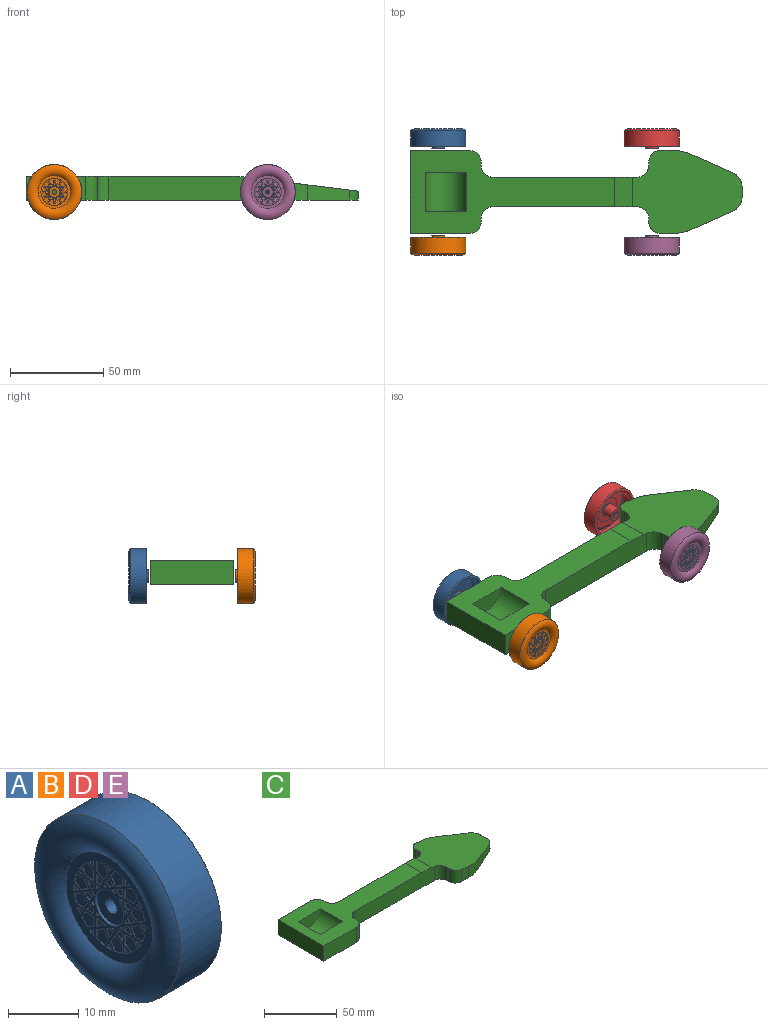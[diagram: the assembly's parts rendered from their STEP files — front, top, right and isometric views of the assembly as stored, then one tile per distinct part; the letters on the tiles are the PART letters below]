
ASSEMBLY  parts=5 mates=3
PART A: 271 faces, bbox 10.7x34x34 mm
  f0: torus R=13.96mm, axis (1,0,0), area 222.7mm2, adj f99,f270
  f1: plane 29.46x29.46mm, normal (-1,0,0), area 2.9mm2, adj f100,f270
  f2: cylinder r=7.18mm len=1.54mm, axis (-1,0,0), area 0.2mm2, adj f27,f86,f101,f256
  f3: cylinder r=7.18mm len=1.05mm, axis (-1,0,0), area 0.1mm2, adj f28,f101,f254,f255
  f4: cylinder r=7.18mm len=1.54mm, axis (-1,0,0), area 0.2mm2, adj f29,f101,f250,f253
  f5: cylinder r=7.18mm len=0.91mm, axis (-1,0,0), area 0.1mm2, adj f30,f101,f248,f249
  f6: cylinder r=7.18mm len=1.13mm, axis (-1,0,0), area 0.2mm2, adj f31,f101,f244,f247
  f7: cylinder r=7.18mm len=0.91mm, axis (-1,0,0), area 0.1mm2, adj f32,f101,f242,f243
  f8: cylinder r=7.18mm len=1.54mm, axis (-1,0,0), area 0.2mm2, adj f33,f101,f238,f241
  f9: cylinder r=7.18mm len=1.05mm, axis (-1,0,0), area 0.1mm2, adj f34,f101,f236,f237
  f10: cylinder r=7.18mm len=1.54mm, axis (-1,0,0), area 0.2mm2, adj f35,f101,f232,f235
  f11: cylinder r=7.18mm len=0.91mm, axis (-1,0,0), area 0.1mm2, adj f36,f101,f230,f231
  f12: cylinder r=7.18mm len=1.13mm, axis (-1,0,0), area 0.2mm2, adj f37,f101,f226,f229
  f13: cylinder r=7.18mm len=0.91mm, axis (-1,0,0), area 0.1mm2, adj f38,f101,f224,f225
  f14: cylinder r=7.18mm len=1.54mm, axis (-1,0,0), area 0.2mm2, adj f39,f101,f220,f223
  f15: cylinder r=7.18mm len=1.05mm, axis (-1,0,0), area 0.1mm2, adj f40,f101,f218,f219
  f16: cylinder r=7.18mm len=1.54mm, axis (-1,0,0), area 0.2mm2, adj f41,f82,f101,f217
  f17: cylinder r=7.18mm len=0.91mm, axis (-1,0,0), area 0.1mm2, adj f65,f101,f118,f139
  f18: cylinder r=7.18mm len=1.13mm, axis (-1,0,0), area 0.2mm2, adj f59,f101,f136,f261
  f19: cylinder r=7.18mm len=1.54mm, axis (-1,0,0), area 0.2mm2, adj f64,f101,f119,f134
  f20: cylinder r=7.18mm len=1.05mm, axis (-1,0,0), area 0.1mm2, adj f53,f101,f132,f133
  f21: cylinder r=7.18mm len=1.54mm, axis (-1,0,0), area 0.2mm2, adj f54,f101,f128,f131
  f22: cylinder r=7.18mm len=0.91mm, axis (-1,0,0), area 0.1mm2, adj f55,f101,f126,f127
  f23: cylinder r=7.18mm len=1.13mm, axis (-1,0,0), area 0.2mm2, adj f56,f101,f125,f142
  f24: cylinder r=7.18mm len=0.91mm, axis (-1,0,0), area 0.1mm2, adj f57,f89,f101,f143
  f25: cylinder r=7.18mm len=0.91mm, axis (-1,0,0), area 0.1mm2, adj f58,f78,f101,f260
  f26: plane 1.41x1.22mm, normal (-1,0,0), area 1.1mm2, adj f85,f146,f147,f258
  f27: plane 2.83x2.32mm, normal (-1,0,0), area 4.5mm2, adj f2,f86,f148,f256,f257
  f28: plane 1.05x0.93mm, normal (-1,0,0), area 0.5mm2, adj f3,f254,f255
  f29: plane 2.83x2.32mm, normal (-1,0,0), area 4.5mm2, adj f4,f250,f251,f252,f253
  f30: plane 1.05x0.91mm, normal (-1,0,0), area 0.5mm2, adj f5,f248,f249
  f31: plane 2.48x2.48mm, normal (-1,0,0), area 4.5mm2, adj f6,f244,f245,f246,f247
  f32: plane 1.05x0.91mm, normal (-1,0,0), area 0.5mm2, adj f7,f242,f243
  f33: plane 2.83x2.32mm, normal (-1,0,0), area 4.5mm2, adj f8,f238,f239,f240,f241
  f34: plane 1.05x0.93mm, normal (-1,0,0), area 0.5mm2, adj f9,f236,f237
  f35: plane 2.83x2.32mm, normal (-1,0,0), area 4.5mm2, adj f10,f232,f233,f234,f235
  f36: plane 1.05x0.91mm, normal (-1,0,0), area 0.5mm2, adj f11,f230,f231
  f37: plane 2.48x2.48mm, normal (-1,0,0), area 4.5mm2, adj f12,f226,f227,f228,f229
  f38: plane 1.05x0.91mm, normal (-1,0,0), area 0.5mm2, adj f13,f224,f225
  f39: plane 2.83x2.32mm, normal (-1,0,0), area 4.5mm2, adj f14,f220,f221,f222,f223
  f40: plane 1.05x0.93mm, normal (-1,0,0), area 0.5mm2, adj f15,f218,f219
  f41: plane 2.83x2.32mm, normal (-1,0,0), area 4.5mm2, adj f16,f82,f152,f216,f217
  f42: plane 0.71x0.45mm, normal (-1,0,0), area 0.2mm2, adj f66,f169,f170,f214,f215
  f43: plane 0.71x0.45mm, normal (-1,0,0), area 0.2mm2, adj f67,f167,f168,f212,f213
  f44: plane 0.52x0.52mm, normal (-1,0,0), area 0.2mm2, adj f68,f165,f166,f210,f211
  f45: plane 0.71x0.45mm, normal (-1,0,0), area 0.2mm2, adj f69,f163,f164,f208,f209
  f46: plane 0.71x0.45mm, normal (-1,0,0), area 0.2mm2, adj f70,f161,f162,f206,f207
  f47: plane 0.52x0.52mm, normal (-1,0,0), area 0.2mm2, adj f71,f159,f160,f204,f205
  f48: plane 0.71x0.45mm, normal (-1,0,0), area 0.2mm2, adj f72,f157,f158,f202,f203
  f49: plane 0.71x0.45mm, normal (-1,0,0), area 0.2mm2, adj f73,f155,f156,f200,f201
  f50: plane 0.52x0.52mm, normal (-1,0,0), area 0.2mm2, adj f74,f87,f144,f145,f154
  f51: plane 1.41x1.22mm, normal (-1,0,0), area 1.1mm2, adj f83,f150,f151,f171
  f52: plane 0.52x0.52mm, normal (-1,0,0), area 0.2mm2, adj f75,f84,f149,f153,f259
  f53: plane 1.05x0.93mm, normal (-1,0,0), area 0.5mm2, adj f20,f132,f133
  f54: plane 2.83x2.32mm, normal (-1,0,0), area 4.5mm2, adj f21,f128,f129,f130,f131
  f55: plane 1.05x0.91mm, normal (-1,0,0), area 0.5mm2, adj f22,f126,f127
  f56: plane 2.48x2.48mm, normal (-1,0,0), area 4.5mm2, adj f23,f88,f108,f125,f142
  f57: plane 1.05x0.91mm, normal (-1,0,0), area 0.5mm2, adj f24,f89,f143
  f58: plane 1.05x0.91mm, normal (-1,0,0), area 0.5mm2, adj f25,f78,f260
  f59: plane 2.48x2.48mm, normal (-1,0,0), area 4.5mm2, adj f18,f79,f115,f136,f261
  f60: plane 1.41x1.22mm, normal (-1,0,0), area 1.1mm2, adj f90,f109,f110,f124
  f61: plane 0.71x0.45mm, normal (-1,0,0), area 0.2mm2, adj f76,f91,f111,f117,f123
  f62: plane 0.71x0.45mm, normal (-1,0,0), area 0.2mm2, adj f77,f81,f113,f116,f138
  f63: plane 1.41x1.22mm, normal (-1,0,0), area 1.1mm2, adj f80,f112,f114,f137
  f64: plane 2.83x2.32mm, normal (-1,0,0), area 4.5mm2, adj f19,f119,f121,f134,f140
  f65: plane 1.05x0.91mm, normal (-1,0,0), area 0.5mm2, adj f17,f118,f139
  f66: cylinder r=3.25mm len=0.13mm, axis (-1,0,0), area 0mm2, adj f42,f101,f169,f170
  f67: cylinder r=3.25mm len=0.13mm, axis (-1,0,0), area 0mm2, adj f43,f101,f167,f168
  f68: cylinder r=3.25mm len=0.13mm, axis (-1,0,0), area 0mm2, adj f44,f101,f165,f166
  f69: cylinder r=3.25mm len=0.13mm, axis (-1,0,0), area 0mm2, adj f45,f101,f163,f164
  f70: cylinder r=3.25mm len=0.13mm, axis (-1,0,0), area 0mm2, adj f46,f101,f161,f162
  f71: cylinder r=3.25mm len=0.13mm, axis (-1,0,0), area 0mm2, adj f47,f101,f159,f160
  f72: cylinder r=3.25mm len=0.13mm, axis (-1,0,0), area 0mm2, adj f48,f101,f157,f158
  f73: cylinder r=3.25mm len=0.13mm, axis (-1,0,0), area 0mm2, adj f49,f101,f155,f156
  f74: cylinder r=3.25mm len=0.13mm, axis (-1,0,0), area 0mm2, adj f50,f101,f144,f154
  f75: cylinder r=3.25mm len=0.13mm, axis (-1,0,0), area 0mm2, adj f52,f101,f153,f259
  f76: cylinder r=3.25mm len=0.13mm, axis (-1,0,0), area 0mm2, adj f61,f91,f101,f117
  f77: cylinder r=3.25mm len=0.13mm, axis (-1,0,0), area 0mm2, adj f62,f81,f101,f116
  f78: plane 1.05x0.13mm, normal (0,1,0), area 0.1mm2, adj f25,f58,f101,f260
  f79: plane 1.7x0.13mm, normal (0,1,0), area 0.2mm2, adj f59,f101,f115,f261
  f80: plane 0.81x0.13mm, normal (0,1,0), area 0.1mm2, adj f63,f101,f112,f114
  f81: plane 0.32x0.13mm, normal (0,1,0), area 0mm2, adj f62,f77,f101,f113
  f82: plane 1.56x0.13mm, normal (0,-1,0), area 0.2mm2, adj f16,f41,f101,f152
  f83: plane 1.41x0.13mm, normal (0,-1,0), area 0.2mm2, adj f51,f101,f150,f151
  f84: plane 0.52x0.13mm, normal (0,-1,0), area 0.1mm2, adj f52,f101,f149,f259
  f85: plane 1.41x0.13mm, normal (0,-1,0), area 0.2mm2, adj f26,f101,f146,f147
  f86: plane 1.56x0.13mm, normal (0,-1,0), area 0.2mm2, adj f2,f27,f101,f148
  f87: plane 0.52x0.13mm, normal (0,-1,0), area 0.1mm2, adj f50,f101,f144,f145
  f88: plane 1.7x0.13mm, normal (0,1,0), area 0.2mm2, adj f56,f101,f108,f142
  f89: plane 1.05x0.13mm, normal (0,1,0), area 0.1mm2, adj f24,f57,f101,f143
  f90: plane 0.81x0.13mm, normal (0,1,0), area 0.1mm2, adj f60,f101,f109,f110
  f91: plane 0.32x0.13mm, normal (0,1,0), area 0mm2, adj f61,f76,f101,f111
  f92: cylinder r=3.49mm len=6.99mm, axis (1,0,0), area 138.2mm2, adj f93,f107
  f93: torus R=3.87mm, axis (1,0,0), area 13.7mm2, adj f92,f94
  f94: plane 14.29x14.29mm, normal (1,0,0), area 113.2mm2, adj f93,f95
  f95: cylinder r=7.14mm len=14.29mm, axis (1,0,0), area 9.1mm2, adj f94,f96
  f96: plane 21.34x21.34mm, normal (1,0,0), area 197.2mm2, adj f95,f97
  f97: cone r=10.67mm half-angle=61deg, axis (-1,0,0), area 132.9mm2, adj f96,f98
  f98: torus R=12.47mm, axis (1,0,0), area 62.7mm2, adj f97,f99
  f99: cylinder r=12.85mm len=25.69mm, axis (1,0,0), area 432.6mm2, adj f0,f98
  f100: torus R=11.88mm, axis (1,0,0), area 499.7mm2, adj f1,f101
  f101: plane 17.53x17.53mm, normal (-1,0,0), area 139.6mm2, adj f2,f3,f4,f5,f6,f7,f8,f9
  f102: cylinder r=2.87mm len=5.74mm, axis (1,0,0), area 6.9mm2, adj f101,f103
  f103: plane 5.74x5.74mm, normal (-1,0,0), area 21.8mm2, adj f102,f104
  f104: cylinder r=1.14mm len=7.19mm, axis (1,0,0), area 51.6mm2, adj f103,f105
  f105: plane 3.61x3.61mm, normal (1,0,0), area 6.1mm2, adj f104,f106
  f106: cylinder r=1.8mm len=3.61mm, axis (1,0,0), area 17.3mm2, adj f105,f107
  f107: plane 6.99x6.99mm, normal (1,0,0), area 28.1mm2, adj f92,f106
  f108: plane 1.7x0.13mm, normal (0,0,1), area 0.2mm2, adj f56,f88,f101,f125
  f109: plane 1.41x0.13mm, normal (0,0,-1), area 0.2mm2, adj f60,f90,f101,f124
  f110: plane 0.7x0.41mm, normal (0,0.5,0.87), area 0.1mm2, adj f60,f90,f101,f124
  f111: plane 0.45x0.26mm, normal (0,-0.5,-0.87), area 0.1mm2, adj f61,f91,f101,f123
  f112: plane 0.7x0.41mm, normal (0,0.5,-0.87), area 0.1mm2, adj f63,f80,f101,f137
  f113: plane 0.45x0.26mm, normal (0,-0.5,0.87), area 0.1mm2, adj f62,f81,f101,f138
  f114: plane 1.41x0.13mm, normal (0,0,1), area 0.2mm2, adj f63,f80,f101,f137
  f115: plane 1.7x0.13mm, normal (0,0,-1), area 0.2mm2, adj f59,f79,f101,f136
  f116: plane 0.28x0.16mm, normal (0,0.87,-0.5), area 0mm2, adj f62,f77,f101,f138
  f117: plane 0.28x0.16mm, normal (0,0.87,0.5), area 0mm2, adj f61,f76,f101,f123
  f118: plane 1.05x0.13mm, normal (0,0,-1), area 0.1mm2, adj f17,f65,f101,f139
  f119: plane 1.56x0.13mm, normal (0,0,1), area 0.2mm2, adj f19,f64,f101,f140
  f120: plane 1.22x0.7mm, normal (0,-0.5,0.87), area 0.2mm2, adj f101,f135,f141,f262
  f121: plane 1.47x0.85mm, normal (0,0.5,-0.87), area 0.2mm2, adj f64,f101,f134,f140
  f122: plane 0.7x0.41mm, normal (0,0.87,-0.5), area 0.1mm2, adj f101,f135,f141,f262
  f123: plane 0.45x0.26mm, normal (0,-0.87,0.5), area 0.1mm2, adj f61,f101,f111,f117
  f124: plane 1.22x0.7mm, normal (0,-0.87,0.5), area 0.2mm2, adj f60,f101,f109,f110
  f125: plane 1.35x0.78mm, normal (0,-0.87,0.5), area 0.2mm2, adj f23,f56,f101,f108
  f126: plane 0.91x0.52mm, normal (0,0.87,-0.5), area 0.1mm2, adj f22,f55,f101,f127
  f127: plane 1.05x0.13mm, normal (0,0,1), area 0.1mm2, adj f22,f55,f101,f126
  f128: plane 1.56x0.13mm, normal (0,0,-1), area 0.2mm2, adj f21,f54,f101,f129
  f129: plane 1.47x0.85mm, normal (0,0.87,-0.5), area 0.2mm2, adj f54,f101,f128,f130
  f130: plane 1.47x0.85mm, normal (0,0.5,0.87), area 0.2mm2, adj f54,f101,f129,f131
  f131: plane 1.35x0.78mm, normal (0,-0.5,0.87), area 0.2mm2, adj f21,f54,f101,f130
  f132: plane 0.91x0.52mm, normal (0,0.5,-0.87), area 0.1mm2, adj f20,f53,f101,f133
  f133: plane 0.91x0.52mm, normal (0,0.5,0.87), area 0.1mm2, adj f20,f53,f101,f132
  f134: plane 1.35x0.78mm, normal (0,-0.5,-0.87), area 0.2mm2, adj f19,f64,f101,f121
  f135: plane 1.22x0.7mm, normal (0,-0.5,-0.87), area 0.2mm2, adj f101,f120,f122,f262
  f136: plane 1.35x0.78mm, normal (0,-0.87,-0.5), area 0.2mm2, adj f18,f59,f101,f115
  f137: plane 1.22x0.7mm, normal (0,-0.87,-0.5), area 0.2mm2, adj f63,f101,f112,f114
  f138: plane 0.45x0.26mm, normal (0,-0.87,-0.5), area 0.1mm2, adj f62,f101,f113,f116
  f139: plane 0.91x0.52mm, normal (0,0.87,0.5), area 0.1mm2, adj f17,f65,f101,f118
  f140: plane 1.47x0.85mm, normal (0,0.87,0.5), area 0.2mm2, adj f64,f101,f119,f121
  f141: plane 0.7x0.41mm, normal (0,0.87,0.5), area 0.1mm2, adj f101,f120,f122,f262
  f142: plane 1.35x0.78mm, normal (0,0.5,-0.87), area 0.2mm2, adj f23,f56,f88,f101
  f143: plane 0.91x0.52mm, normal (0,-0.5,0.87), area 0.1mm2, adj f24,f57,f89,f101
  f144: plane 0.28x0.16mm, normal (0,0.5,0.87), area 0mm2, adj f50,f74,f87,f101
  f145: plane 0.52x0.13mm, normal (0,0,-1), area 0.1mm2, adj f50,f87,f101,f154
  f146: plane 0.81x0.13mm, normal (0,0,1), area 0.1mm2, adj f26,f85,f101,f258
  f147: plane 1.22x0.7mm, normal (0,0.5,-0.87), area 0.2mm2, adj f26,f85,f101,f258
  f148: plane 1.47x0.85mm, normal (0,-0.5,0.87), area 0.2mm2, adj f27,f86,f101,f257
  f149: plane 0.52x0.13mm, normal (0,0,1), area 0.1mm2, adj f52,f84,f101,f153
  f150: plane 0.81x0.13mm, normal (0,0,-1), area 0.1mm2, adj f51,f83,f101,f171
  f151: plane 1.22x0.7mm, normal (0,0.5,0.87), area 0.2mm2, adj f51,f83,f101,f171
  f152: plane 1.47x0.85mm, normal (0,-0.5,-0.87), area 0.2mm2, adj f41,f82,f101,f216
  f153: plane 0.28x0.16mm, normal (0,0.87,-0.5), area 0mm2, adj f52,f75,f101,f149
  f154: plane 0.28x0.16mm, normal (0,0.87,0.5), area 0mm2, adj f50,f74,f101,f145
  f155: plane 0.32x0.13mm, normal (0,0,1), area 0mm2, adj f49,f73,f101,f200
  f156: plane 0.28x0.16mm, normal (0,0.5,0.87), area 0mm2, adj f49,f73,f101,f201
  f157: plane 0.28x0.16mm, normal (0,-0.5,0.87), area 0mm2, adj f48,f72,f101,f202
  f158: plane 0.32x0.13mm, normal (0,0,1), area 0mm2, adj f48,f72,f101,f203
  f159: plane 0.28x0.16mm, normal (0,-0.87,0.5), area 0mm2, adj f47,f71,f101,f204
  f160: plane 0.28x0.16mm, normal (0,-0.5,0.87), area 0mm2, adj f47,f71,f101,f205
  f161: plane 0.32x0.13mm, normal (0,-1,0), area 0mm2, adj f46,f70,f101,f206
  f162: plane 0.28x0.16mm, normal (0,-0.87,0.5), area 0mm2, adj f46,f70,f101,f207
  f163: plane 0.28x0.16mm, normal (0,-0.87,-0.5), area 0mm2, adj f45,f69,f101,f208
  f164: plane 0.32x0.13mm, normal (0,-1,0), area 0mm2, adj f45,f69,f101,f209
  f165: plane 0.28x0.16mm, normal (0,-0.5,-0.87), area 0mm2, adj f44,f68,f101,f210
  f166: plane 0.28x0.16mm, normal (0,-0.87,-0.5), area 0mm2, adj f44,f68,f101,f211
  f167: plane 0.32x0.13mm, normal (0,0,-1), area 0mm2, adj f43,f67,f101,f212
  f168: plane 0.28x0.16mm, normal (0,-0.5,-0.87), area 0mm2, adj f43,f67,f101,f213
  f169: plane 0.28x0.16mm, normal (0,0.5,-0.87), area 0mm2, adj f42,f66,f101,f214
  f170: plane 0.32x0.13mm, normal (0,0,-1), area 0mm2, adj f42,f66,f101,f215
  f171: plane 0.7x0.41mm, normal (0,0.87,-0.5), area 0.1mm2, adj f51,f101,f150,f151
  f172: plane 0.7x0.41mm, normal (0,-0.87,0.5), area 0.1mm2, adj f101,f173,f175,f263
  f173: plane 1.22x0.7mm, normal (0,-0.5,-0.87), area 0.2mm2, adj f101,f172,f174,f263
  f174: plane 1.41x0.13mm, normal (0,1,0), area 0.2mm2, adj f101,f173,f175,f263
  f175: plane 0.81x0.13mm, normal (0,0,1), area 0.1mm2, adj f101,f172,f174,f263
  f176: plane 0.7x0.41mm, normal (0,-0.87,-0.5), area 0.1mm2, adj f101,f177,f179,f264
  f177: plane 1.22x0.7mm, normal (0,0.5,-0.87), area 0.2mm2, adj f101,f176,f178,f264
  f178: plane 1.22x0.7mm, normal (0,0.5,0.87), area 0.2mm2, adj f101,f177,f179,f264
  f179: plane 0.7x0.41mm, normal (0,-0.87,0.5), area 0.1mm2, adj f101,f176,f178,f264
  f180: plane 0.81x0.13mm, normal (0,0,-1), area 0.1mm2, adj f101,f181,f183,f265
  f181: plane 1.41x0.13mm, normal (0,1,0), area 0.2mm2, adj f101,f180,f182,f265
  f182: plane 1.22x0.7mm, normal (0,-0.5,0.87), area 0.2mm2, adj f101,f181,f183,f265
  f183: plane 0.7x0.41mm, normal (0,-0.87,-0.5), area 0.1mm2, adj f101,f180,f182,f265
  f184: plane 0.7x0.41mm, normal (0,0.5,-0.87), area 0.1mm2, adj f101,f185,f187,f266
  f185: plane 1.22x0.7mm, normal (0,0.87,0.5), area 0.2mm2, adj f101,f184,f186,f266
  f186: plane 1.22x0.7mm, normal (0,-0.87,0.5), area 0.2mm2, adj f101,f185,f187,f266
  f187: plane 0.7x0.41mm, normal (0,-0.5,-0.87), area 0.1mm2, adj f101,f184,f186,f266
  f188: plane 0.7x0.41mm, normal (0,-0.5,-0.87), area 0.1mm2, adj f101,f189,f191,f267
  f189: plane 1.22x0.7mm, normal (0,0.87,-0.5), area 0.2mm2, adj f101,f188,f190,f267
  f190: plane 1.41x0.13mm, normal (0,0,1), area 0.2mm2, adj f101,f189,f191,f267
  f191: plane 0.81x0.13mm, normal (0,-1,0), area 0.1mm2, adj f101,f188,f190,f267
  f192: plane 0.81x0.13mm, normal (0,-1,0), area 0.1mm2, adj f101,f193,f195,f268
  f193: plane 1.41x0.13mm, normal (0,0,-1), area 0.2mm2, adj f101,f192,f194,f268
  f194: plane 1.22x0.7mm, normal (0,0.87,0.5), area 0.2mm2, adj f101,f193,f195,f268
  f195: plane 0.7x0.41mm, normal (0,-0.5,0.87), area 0.1mm2, adj f101,f192,f194,f268
  f196: plane 0.7x0.41mm, normal (0,-0.5,0.87), area 0.1mm2, adj f101,f197,f199,f269
  f197: plane 1.22x0.7mm, normal (0,-0.87,-0.5), area 0.2mm2, adj f101,f196,f198,f269
  f198: plane 1.22x0.7mm, normal (0,0.87,-0.5), area 0.2mm2, adj f101,f197,f199,f269
  f199: plane 0.7x0.41mm, normal (0,0.5,0.87), area 0.1mm2, adj f101,f196,f198,f269
  f200: plane 0.45x0.26mm, normal (0,-0.87,-0.5), area 0.1mm2, adj f49,f101,f155,f201
  f201: plane 0.45x0.26mm, normal (0,0.5,-0.87), area 0.1mm2, adj f49,f101,f156,f200
  f202: plane 0.45x0.26mm, normal (0,-0.5,-0.87), area 0.1mm2, adj f48,f101,f157,f203
  f203: plane 0.45x0.26mm, normal (0,0.87,-0.5), area 0.1mm2, adj f48,f101,f158,f202
  f204: plane 0.52x0.13mm, normal (0,0,-1), area 0.1mm2, adj f47,f101,f159,f205
  f205: plane 0.52x0.13mm, normal (0,1,0), area 0.1mm2, adj f47,f101,f160,f204
  f206: plane 0.45x0.26mm, normal (0,0.5,-0.87), area 0.1mm2, adj f46,f101,f161,f207
  f207: plane 0.45x0.26mm, normal (0,0.87,0.5), area 0.1mm2, adj f46,f101,f162,f206
  f208: plane 0.45x0.26mm, normal (0,0.87,-0.5), area 0.1mm2, adj f45,f101,f163,f209
  f209: plane 0.45x0.26mm, normal (0,0.5,0.87), area 0.1mm2, adj f45,f101,f164,f208
  f210: plane 0.52x0.13mm, normal (0,1,0), area 0.1mm2, adj f44,f101,f165,f211
  f211: plane 0.52x0.13mm, normal (0,0,1), area 0.1mm2, adj f44,f101,f166,f210
  f212: plane 0.45x0.26mm, normal (0,0.87,0.5), area 0.1mm2, adj f43,f101,f167,f213
  f213: plane 0.45x0.26mm, normal (0,-0.5,0.87), area 0.1mm2, adj f43,f101,f168,f212
  f214: plane 0.45x0.26mm, normal (0,0.5,0.87), area 0.1mm2, adj f42,f101,f169,f215
  f215: plane 0.45x0.26mm, normal (0,-0.87,0.5), area 0.1mm2, adj f42,f101,f170,f214
  f216: plane 1.47x0.85mm, normal (0,0.87,-0.5), area 0.2mm2, adj f41,f101,f152,f217
  f217: plane 1.35x0.78mm, normal (0,0.87,0.5), area 0.2mm2, adj f16,f41,f101,f216
  f218: plane 0.91x0.52mm, normal (0,-0.87,-0.5), area 0.1mm2, adj f15,f40,f101,f219
  f219: plane 0.91x0.52mm, normal (0,0.87,-0.5), area 0.1mm2, adj f15,f40,f101,f218
  f220: plane 1.35x0.78mm, normal (0,-0.87,0.5), area 0.2mm2, adj f14,f39,f101,f221
  f221: plane 1.47x0.85mm, normal (0,-0.87,-0.5), area 0.2mm2, adj f39,f101,f220,f222
  f222: plane 1.47x0.85mm, normal (0,0.5,-0.87), area 0.2mm2, adj f39,f101,f221,f223
  f223: plane 1.56x0.13mm, normal (0,1,0), area 0.2mm2, adj f14,f39,f101,f222
  f224: plane 1.05x0.13mm, normal (0,-1,0), area 0.1mm2, adj f13,f38,f101,f225
  f225: plane 0.91x0.52mm, normal (0,0.5,-0.87), area 0.1mm2, adj f13,f38,f101,f224
  f226: plane 1.35x0.78mm, normal (0,-0.5,0.87), area 0.2mm2, adj f12,f37,f101,f227
  f227: plane 1.7x0.13mm, normal (0,-1,0), area 0.2mm2, adj f37,f101,f226,f228
  f228: plane 1.7x0.13mm, normal (0,0,-1), area 0.2mm2, adj f37,f101,f227,f229
  f229: plane 1.35x0.78mm, normal (0,0.87,-0.5), area 0.2mm2, adj f12,f37,f101,f228
  f230: plane 0.91x0.52mm, normal (0,-0.87,0.5), area 0.1mm2, adj f11,f36,f101,f231
  f231: plane 1.05x0.13mm, normal (0,0,-1), area 0.1mm2, adj f11,f36,f101,f230
  f232: plane 1.56x0.13mm, normal (0,0,1), area 0.2mm2, adj f10,f35,f101,f233
  f233: plane 1.47x0.85mm, normal (0,-0.87,0.5), area 0.2mm2, adj f35,f101,f232,f234
  f234: plane 1.47x0.85mm, normal (0,-0.5,-0.87), area 0.2mm2, adj f35,f101,f233,f235
  f235: plane 1.35x0.78mm, normal (0,0.5,-0.87), area 0.2mm2, adj f10,f35,f101,f234
  f236: plane 0.91x0.52mm, normal (0,-0.5,0.87), area 0.1mm2, adj f9,f34,f101,f237
  f237: plane 0.91x0.52mm, normal (0,-0.5,-0.87), area 0.1mm2, adj f9,f34,f101,f236
  f238: plane 1.35x0.78mm, normal (0,0.5,0.87), area 0.2mm2, adj f8,f33,f101,f239
  f239: plane 1.47x0.85mm, normal (0,-0.5,0.87), area 0.2mm2, adj f33,f101,f238,f240
  f240: plane 1.47x0.85mm, normal (0,-0.87,-0.5), area 0.2mm2, adj f33,f101,f239,f241
  f241: plane 1.56x0.13mm, normal (0,0,-1), area 0.2mm2, adj f8,f33,f101,f240
  f242: plane 1.05x0.13mm, normal (0,0,1), area 0.1mm2, adj f7,f32,f101,f243
  f243: plane 0.91x0.52mm, normal (0,-0.87,-0.5), area 0.1mm2, adj f7,f32,f101,f242
  f244: plane 1.35x0.78mm, normal (0,0.87,0.5), area 0.2mm2, adj f6,f31,f101,f245
  f245: plane 1.7x0.13mm, normal (0,0,1), area 0.2mm2, adj f31,f101,f244,f246
  f246: plane 1.7x0.13mm, normal (0,-1,0), area 0.2mm2, adj f31,f101,f245,f247
  f247: plane 1.35x0.78mm, normal (0,-0.5,-0.87), area 0.2mm2, adj f6,f31,f101,f246
  f248: plane 0.91x0.52mm, normal (0,0.5,0.87), area 0.1mm2, adj f5,f30,f101,f249
  f249: plane 1.05x0.13mm, normal (0,-1,0), area 0.1mm2, adj f5,f30,f101,f248
  f250: plane 1.56x0.13mm, normal (0,1,0), area 0.2mm2, adj f4,f29,f101,f251
  f251: plane 1.47x0.85mm, normal (0,0.5,0.87), area 0.2mm2, adj f29,f101,f250,f252
  f252: plane 1.47x0.85mm, normal (0,-0.87,0.5), area 0.2mm2, adj f29,f101,f251,f253
  f253: plane 1.35x0.78mm, normal (0,-0.87,-0.5), area 0.2mm2, adj f4,f29,f101,f252
  f254: plane 0.91x0.52mm, normal (0,0.87,0.5), area 0.1mm2, adj f3,f28,f101,f255
  f255: plane 0.91x0.52mm, normal (0,-0.87,0.5), area 0.1mm2, adj f3,f28,f101,f254
  f256: plane 1.35x0.78mm, normal (0,0.87,-0.5), area 0.2mm2, adj f2,f27,f101,f257
  f257: plane 1.47x0.85mm, normal (0,0.87,0.5), area 0.2mm2, adj f27,f101,f148,f256
  f258: plane 0.7x0.41mm, normal (0,0.87,0.5), area 0.1mm2, adj f26,f101,f146,f147
  f259: plane 0.28x0.16mm, normal (0,0.5,-0.87), area 0mm2, adj f52,f75,f84,f101
  f260: plane 0.91x0.52mm, normal (0,-0.5,-0.87), area 0.1mm2, adj f25,f58,f78,f101
  f261: plane 1.35x0.78mm, normal (0,0.5,0.87), area 0.2mm2, adj f18,f59,f79,f101
  f262: plane 1.63x1.41mm, normal (-1,0,0), area 1.1mm2, adj f120,f122,f135,f141
  f263: plane 1.41x1.22mm, normal (-1,0,0), area 1.1mm2, adj f172,f173,f174,f175
  f264: plane 1.63x1.41mm, normal (-1,0,0), area 1.1mm2, adj f176,f177,f178,f179
  f265: plane 1.41x1.22mm, normal (-1,0,0), area 1.1mm2, adj f180,f181,f182,f183
  f266: plane 1.63x1.41mm, normal (-1,0,0), area 1.1mm2, adj f184,f185,f186,f187
  f267: plane 1.41x1.22mm, normal (-1,0,0), area 1.1mm2, adj f188,f189,f190,f191
  f268: plane 1.41x1.22mm, normal (-1,0,0), area 1.1mm2, adj f192,f193,f194,f195
  f269: plane 1.63x1.41mm, normal (-1,0,0), area 1.1mm2, adj f196,f197,f198,f199
  f270: cylinder r=14.73mm len=29.46mm, axis (1,0,0), area 756.9mm2, adj f0,f1
PART B: same geometry as A
PART C: 33 faces, bbox 177.8x44.5x12.7 mm
  f0: plane 31.75x12.7mm, normal (0,1,0), area 403.2mm2, adj f2,f3,f6,f25
  f1: plane 31.75x12.7mm, normal (0,-1,0), area 403.2mm2, adj f2,f3,f6,f18
  f2: plane 177.8x44.45mm, normal (0,0,-1), area 4870.6mm2, adj f0,f1,f4,f5,f6,f7,f8,f9
  f3: plane 109.56x44.45mm, normal (0,0,1), area 2359.6mm2, adj f0,f1,f6,f12,f14,f15,f17,f18
  f4: plane 5.63x4.76mm, normal (1,0,0), area 26.8mm2, adj f2,f26,f28,f29
  f5: plane 10.21x6.35mm, normal (0,1,0), area 62.3mm2, adj f2,f11,f22,f26
  f6: plane 44.45x12.7mm, normal (-1,0,0), area 564.5mm2, adj f0,f1,f2,f3
  f7: plane 10.21x6.35mm, normal (0,-1,0), area 62.3mm2, adj f2,f10,f19,f26
  f8: plane 22.1x9.94mm, normal (0.41,-0.91,0), area 163mm2, adj f2,f10,f26,f28
  f9: plane 22.1x9.94mm, normal (0.41,0.91,0), area 163mm2, adj f2,f11,f26,f29
  f10: cylinder r=25.4mm len=10.42mm, axis (0,0,-1), area 93.9mm2, adj f2,f7,f8,f26
  f11: cylinder r=25.4mm len=10.42mm, axis (0,0,-1), area 93.9mm2, adj f2,f5,f9,f26
  f12: plane 12.7x1.59mm, normal (1,0,0), area 20.2mm2, adj f2,f3,f18,f21
  f13: plane 11x1.59mm, normal (-1,0,0), area 17.5mm2, adj f2,f19,f20,f26
  f14: plane 77.1x12.7mm, normal (0,-1,0), area 975.5mm2, adj f2,f3,f20,f21,f26,f27
  f15: plane 12.7x1.59mm, normal (1,0,0), area 20.2mm2, adj f2,f3,f24,f25
  f16: plane 11x1.59mm, normal (-1,0,0), area 17.5mm2, adj f2,f22,f23,f26
  f17: plane 77.1x12.7mm, normal (0,1,0), area 975.5mm2, adj f2,f3,f23,f24,f26,f27
  f18: cylinder r=6.35mm len=12.7mm, axis (0,0,1), area 126.7mm2, adj f1,f2,f3,f12
  f19: cylinder r=6.35mm len=11mm, axis (0,0,-1), area 106.8mm2, adj f2,f7,f13,f26
  f20: cylinder r=6.35mm len=11.79mm, axis (0,0,1), area 112.6mm2, adj f2,f13,f14,f26
  f21: cylinder r=6.35mm len=12.7mm, axis (0,0,-1), area 126.7mm2, adj f2,f3,f12,f14
  f22: cylinder r=6.35mm len=11mm, axis (0,0,-1), area 106.8mm2, adj f2,f5,f16,f26
  f23: cylinder r=6.35mm len=11.79mm, axis (0,0,1), area 112.6mm2, adj f2,f16,f17,f26
  f24: cylinder r=6.35mm len=12.7mm, axis (0,0,-1), area 126.7mm2, adj f2,f3,f15,f17
  f25: cylinder r=6.35mm len=12.7mm, axis (0,0,1), area 126.7mm2, adj f0,f2,f3,f15
  f26: plane 58.79x44.45mm, normal (0.12,0,0.99), area 1907.4mm2, adj f4,f5,f7,f8,f9,f10,f11,f13
  f27: cylinder r=76.2mm len=15.88mm, axis (0,-1,0), area 150.4mm2, adj f3,f14,f17,f26
  f28: cylinder r=7.94mm len=7.24mm, axis (0,0,-1), area 45.3mm2, adj f2,f4,f8,f26
  f29: cylinder r=7.94mm len=7.24mm, axis (0,0,1), area 45.3mm2, adj f2,f4,f9,f26
  f30: cylinder r=11.05mm len=21.95mm, axis (0,1,0), area 686.3mm2, adj f3,f31,f32
  f31: plane 21.95x9.78mm, normal (0,1,0), area 163.8mm2, adj f3,f30
  f32: plane 21.95x9.78mm, normal (0,-1,0), area 163.8mm2, adj f3,f30
PART D: same geometry as A
PART E: same geometry as A
PLACE A rot(axis=(0.58,-0.58,-0.58),120deg) t=(-73.72,23.28,4.33)mm
PLACE B rot(axis=(-0.58,-0.58,0.58),120deg) t=(-73.72,-23.28,4.33)mm fixed
PLACE C at identity fixed
PLACE D rot(axis=(0.58,-0.58,-0.58),120deg) t=(40.58,23.28,4.33)mm
PLACE E rot(axis=(-0.58,-0.58,0.58),120deg) t=(40.58,-23.28,4.33)mm
MATE planar C.f0 <-> A.f0  axis (0,1,0) through (-73.02,22.22,6.35)mm
MATE parallel C.f0 <-> A.f0  axis (0,1,0) through (-73.02,22.22,6.35)mm
MATE cylindrical A.f270 <-> B.f0  axis (0,-1,0) through (-73.72,28.64,4.33)mm
